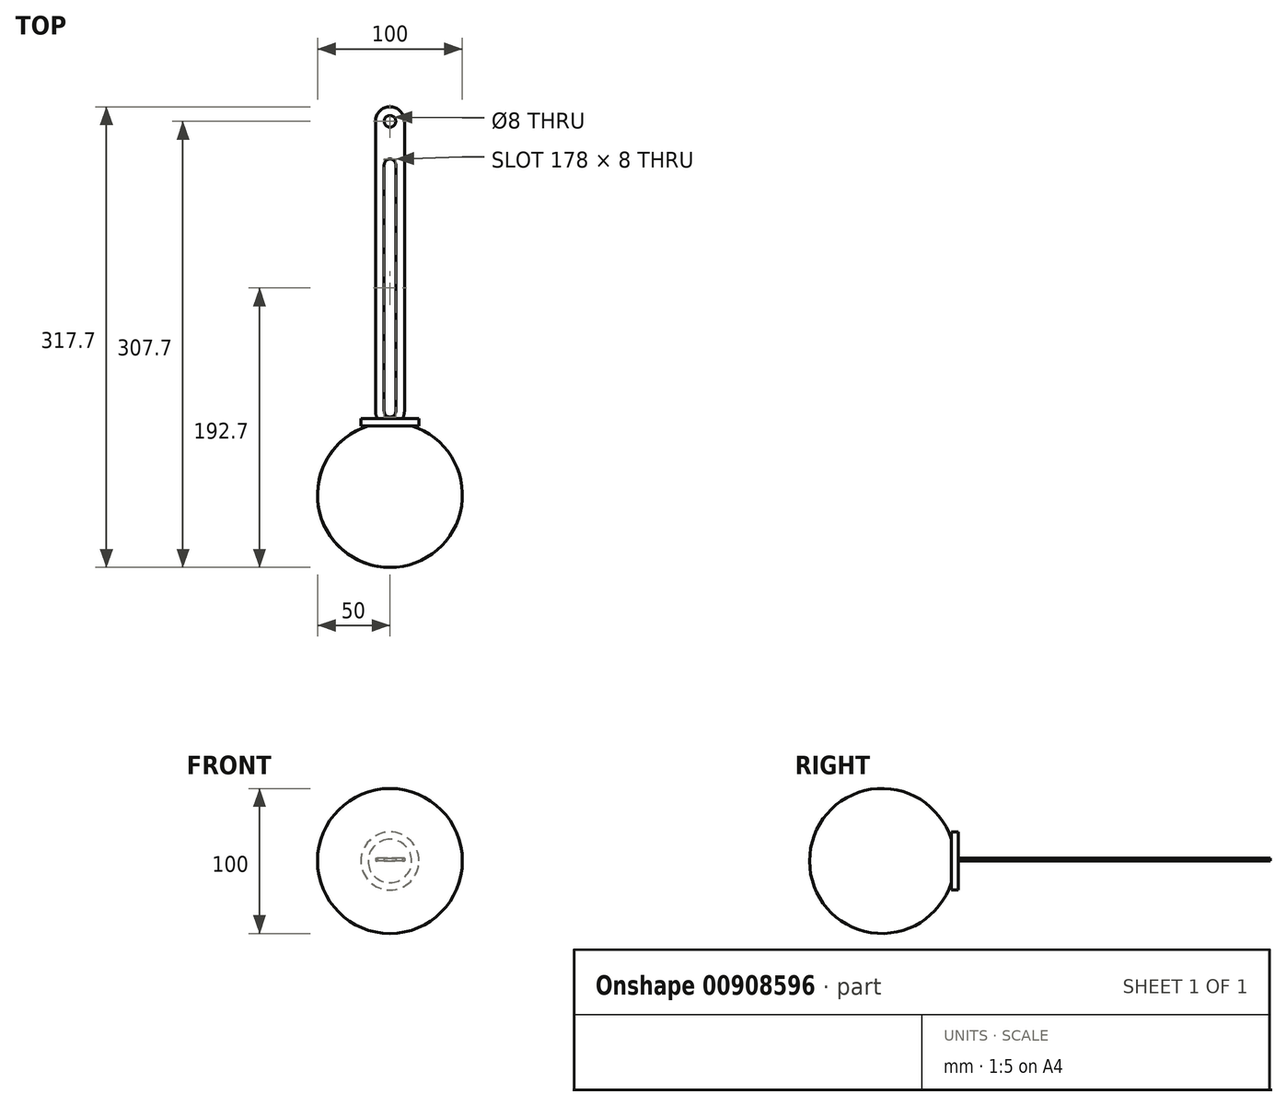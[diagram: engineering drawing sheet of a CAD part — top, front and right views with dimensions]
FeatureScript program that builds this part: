
annotation { "Feature Type Name" : "Feature", "Feature Type Description" : "" }
export const myFeature = defineFeature(function(context is Context, id is Id, definition is map)
    precondition{}
    {
        {
            var Q0;
            Q0=qCreatedBy(makeId("Top.planeOp"),FACE);
            var sketch = newSketch(context, id + "F0", { "sketchPlane" : qUnion([Q0])});
            skLineSegment(sketch, "E0.bottom", {"start": v(10, 100) * mm, "end": v(-10, 100) * mm});
            skLineSegment(sketch, "E0.top", {"start": v(10, -100) * mm, "end": v(-10, -100) * mm});
            skLineSegment(sketch, "E0.left", {"start": v(10, 100) * mm, "end": v(10, -100) * mm});
            skLineSegment(sketch, "E0.right", {"start": v(-10, 100) * mm, "end": v(-10, -100) * mm});
            skPoint(sketch, "E0.middle", {"position": v(0, 0) * mm});
            skArc(sketch, "E1", {"start": v(-10, 100) * mm, "mid": v(0, 110) * mm, "end": v(10, 100) * mm});
            skArc(sketch, "E2.MirrorCS", {"start": v(-10, -100) * mm, "mid": v(0, -110) * mm, "end": v(10, -100) * mm});
            skSolve(sketch);
        }
        {
            var Q0;
            Q0=qSketchRegion(id+"F0",true);
            extrude(context, id + "F1", {"entities" : qUnion([Q0]), "depth" : 2 * mm, "offsetDistance" : 25 * mm});
        }
        {
            var Q0;
            Q0=qCreatedBy(makeId("Top.planeOp"),FACE);
            var sketch = newSketch(context, id + "F2", { "sketchPlane" : qUnion([Q0])});
            skCircle(sketch, "E3", {"center": v(0, 100) * mm, "radius": 4 * mm});
            skCircle(sketch, "E4", {"center": v(0, 0) * mm, "radius": 4 * mm});
            skCircle(sketch, "E5.MirrorC", {"center": v(0, -100) * mm, "radius": 4 * mm});
            skLineSegment(sketch, "E6.bottom", {"start": v(4, 0) * mm, "end": v(-4, 0) * mm});
            skLineSegment(sketch, "E6.top", {"start": v(4, -100) * mm, "end": v(-4, -100) * mm});
            skLineSegment(sketch, "E6.left", {"start": v(4, 0) * mm, "end": v(4, -100) * mm});
            skLineSegment(sketch, "E6.right", {"start": v(-4, 0) * mm, "end": v(-4, -100) * mm});
            skPoint(sketch, "E6.middle", {"position": v(0, -50) * mm});
            skCircle(sketch, "E7", {"center": v(0, 70) * mm, "radius": 4 * mm});
            skLineSegment(sketch, "E8", {"start": v(4, 0) * mm, "end": v(4, 70) * mm});
            skLineSegment(sketch, "E9", {"start": v(-4, 0) * mm, "end": v(-4, 70) * mm});
            skSolve(sketch);
        }
        {
            var Q0;
            Q0=qSketchRegion(id+"F2",true);
            extrude(context, id + "F3", {"entities" : qUnion([Q0]), "operationType" : NewBodyOperationType.REMOVE, "endBound" : BoundingType.SYMMETRIC, "depth" : 25 * mm, "offsetDistance" : 25 * mm});
        }
        {
            var Q0;
            Q0=qCreatedBy(makeId("Top.planeOp"),FACE);
            var sketch = newSketch(context, id + "F4", { "sketchPlane" : qUnion([Q0])});
            skLineSegment(sketch, "E10.bottom", {"start": v(0, -105) * mm, "end": v(20, -105) * mm});
            skLineSegment(sketch, "E10.top", {"start": v(0, -110) * mm, "end": v(20, -110) * mm});
            skLineSegment(sketch, "E10.left", {"start": v(0, -105) * mm, "end": v(0, -110) * mm});
            skLineSegment(sketch, "E10.right", {"start": v(20, -105) * mm, "end": v(20, -110) * mm});
            skArc(sketch, "E11", {"start": v(15, -110) * mm, "mid": v(49.42, -165.28) * mm, "end": v(0, -207.7) * mm});
            skLineSegment(sketch, "E12", {"start": v(0, -207.7) * mm, "end": v(0, -110) * mm});
            skSolve(sketch);
        }
        {
            var Q0;
            Q0 = qSketchRegion(id + "F4", true);
            var Q1;
            Q1=sQuery(id+"F4.wireOp",EDGE,"E10.left");
            revolve(context, id + "F5", {"operationType" : NewBodyOperationType.ADD, "surfaceOperationType" : NewSurfaceOperationType.NEW, "entities" : qUnion([Q0]), "axis" : qUnion([Q1]), "revolveType" : RevolveType.FULL});
        }
    });
